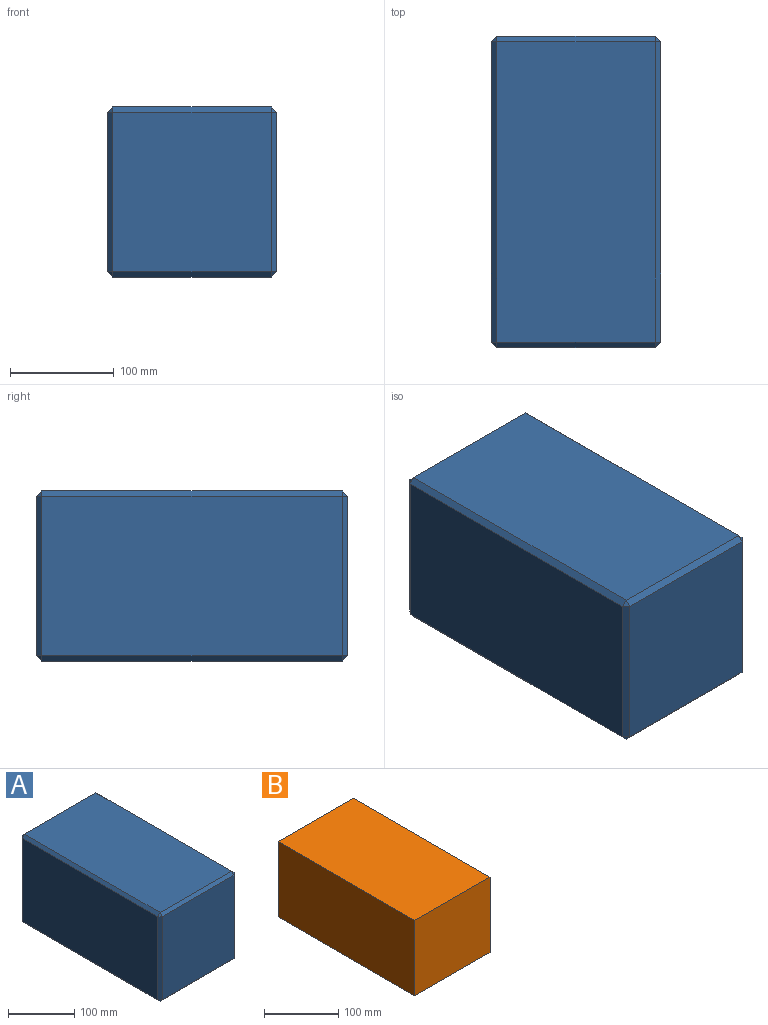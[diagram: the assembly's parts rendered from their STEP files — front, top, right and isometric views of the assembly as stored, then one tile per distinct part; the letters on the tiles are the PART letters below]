
ASSEMBLY  parts=2 mates=3
PART A: 31 faces, bbox 163x300x164 mm
  f0: plane 289.84x153.84mm, normal (1,0,0), area 4269mm2, adj f6,f8,f9,f10,f19,f24,f27,f30
  f1: plane 289.84x152.84mm, normal (0,0,1), area 44299.1mm2, adj f16,f25,f26,f30
  f2: plane 289.84x153.84mm, normal (-1,0,0), area 44589mm2, adj f11,f15,f16,f17
  f3: plane 289.84x152.84mm, normal (0,0,-1), area 44299.1mm2, adj f11,f14,f18,f19
  f4: plane 153.84x152.84mm, normal (0,-1,0), area 23512.9mm2, adj f14,f15,f24,f25
  f5: plane 153.84x152.84mm, normal (0,1,0), area 23512.9mm2, adj f17,f18,f26,f27
  f6: plane 280x153mm, normal (0,0,-1), area 42840mm2, adj f0,f7,f9,f10
  f7: plane 280x144mm, normal (1,0,0), area 40320mm2, adj f6,f8,f9,f10
  f8: plane 280x153mm, normal (0,0,1), area 42840mm2, adj f0,f7,f9,f10
  f9: plane 153x144mm, normal (0,1,0), area 22032mm2, adj f0,f6,f7,f8
  f10: plane 153x144mm, normal (0,-1,0), area 22032mm2, adj f0,f6,f7,f8
  f11: plane 289.84x5.08mm, normal (-0.71,0,-0.71), area 2082.3mm2, adj f2,f3,f12,f13
  f12: plane 5.08x5.08mm, normal (-0.58,-0.58,-0.58), area 22.3mm2, adj f11,f14,f15
  f13: plane 5.08x5.08mm, normal (-0.58,0.58,-0.58), area 22.3mm2, adj f11,f17,f18
  f14: plane 152.84x5.08mm, normal (0,-0.71,-0.71), area 1098mm2, adj f3,f4,f12,f20
  f15: plane 153.84x5.08mm, normal (-0.71,-0.71,0), area 1105.2mm2, adj f2,f4,f12,f21
  f16: plane 289.84x5.08mm, normal (-0.71,0,0.71), area 2082.3mm2, adj f1,f2,f21,f22
  f17: plane 153.84x5.08mm, normal (-0.71,0.71,0), area 1105.2mm2, adj f2,f5,f13,f22
  f18: plane 152.84x5.08mm, normal (0,0.71,-0.71), area 1098mm2, adj f3,f5,f13,f23
  f19: plane 289.84x5.08mm, normal (0.71,0,-0.71), area 2082.3mm2, adj f0,f3,f20,f23
  f20: plane 5.08x5.08mm, normal (0.58,-0.58,-0.58), area 22.3mm2, adj f14,f19,f24
  f21: plane 5.08x5.08mm, normal (-0.58,-0.58,0.58), area 22.3mm2, adj f15,f16,f25
  f22: plane 5.08x5.08mm, normal (-0.58,0.58,0.58), area 22.3mm2, adj f16,f17,f26
  f23: plane 5.08x5.08mm, normal (0.58,0.58,-0.58), area 22.3mm2, adj f18,f19,f27
  f24: plane 153.84x5.08mm, normal (0.71,-0.71,0), area 1105.2mm2, adj f0,f4,f20,f28
  f25: plane 152.84x5.08mm, normal (0,-0.71,0.71), area 1098mm2, adj f1,f4,f21,f28
  f26: plane 152.84x5.08mm, normal (0,0.71,0.71), area 1098mm2, adj f1,f5,f22,f29
  f27: plane 153.84x5.08mm, normal (0.71,0.71,0), area 1105.2mm2, adj f0,f5,f23,f29
  f28: plane 5.08x5.08mm, normal (0.58,-0.58,0.58), area 22.3mm2, adj f24,f25,f30
  f29: plane 5.08x5.08mm, normal (0.58,0.58,0.58), area 22.3mm2, adj f26,f27,f30
  f30: plane 289.84x5.08mm, normal (0.71,0,0.71), area 2082.3mm2, adj f0,f1,f28,f29
PART B: 6 faces, bbox 143x260x124 mm
  f0: plane 260x124mm, normal (1,0,0), area 32240mm2, adj f1,f3,f4,f5
  f1: plane 260x143mm, normal (0,0,1), area 37180mm2, adj f0,f2,f4,f5
  f2: plane 260x124mm, normal (-1,0,0), area 32240mm2, adj f1,f3,f4,f5
  f3: plane 260x143mm, normal (0,0,-1), area 37180mm2, adj f0,f2,f4,f5
  f4: plane 143x124mm, normal (0,-1,0), area 17732mm2, adj f0,f1,f2,f3
  f5: plane 143x124mm, normal (0,1,0), area 17732mm2, adj f0,f1,f2,f3
PLACE A t=(348.47,585.5,-61.74)mm
PLACE B t=(353.47,565.5,-71.74)mm
MATE fastened B.f3 <-> A.f8  axis (0,0,-1) through (353.47,435.5,-133.74)mm
MATE planar B.f3 <-> A.f8  axis (0,0,-1) through (353.47,435.5,-133.74)mm
MATE planar A.f7 <-> B.f2  axis (1,0,0) through (276.97,435.5,-61.74)mm
